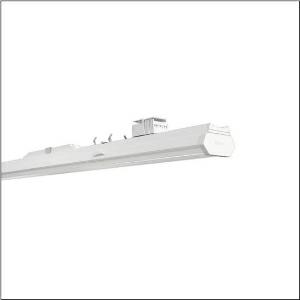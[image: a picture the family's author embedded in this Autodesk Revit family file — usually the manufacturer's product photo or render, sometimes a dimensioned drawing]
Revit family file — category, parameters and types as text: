
# Revit family: licross_21_protected_mo_52td1bdn4axg
name_source: partatom
category: Lighting Fixtures
units: mm (PartAtom-declared; Revit-internal decimal feet)

## family parameters
Cut with Voids When Loaded = No
Host = Face
Light Source = No
Part Type = Normal
Room Calculation Point = No
Round Connector Dimension = Use Diameter
Shared = No

## types (1)
- --- (1 x LED, 10050 lm, 62 W, 4000K)
    Apparent Load = 62 VA
    CIE Flux Codes = 54 82 95 97 100
    Color Rendering = 80
    Color Temperature = 4000K
    Default Elevation = 1800 mm
    Description = Licross 21 Protected MO, luminaire insert, of sheet steel, galvanised, coil coated, white, length: 1.500mm, width: 90mm, height: 103mm, LED rated luminous flux: 10.060lm, light colour: 840, SDCM (Standard Deviation of Colour Matching)MacAdam ≤ 3 SDCM (initial), control gear: DALI 2, with plug, 5-pole, with phase selection, mains connection: 220..240V, AC, 50/60Hz, rated input power: 62W, internal wiring halogen-free, primary optical cover: cover, of PMMA, light emission: direct distribution, primary light characteristic: symmetric, protection rating (complete): IP54, insulation class (complete): insulation class I (protective earthing), certification: CE, ENEC, VDE, UKCA, protection symbol: D if used in an environment with non-conductive dust loads with corresponding accessories, impact resistance: IK06, permissible ambient temperature for indoor applications: -25..+35°C, corresponds to IFS (International Featured Standards) requirements for safety and quality in the food industry, reducing of maximum allowable ambient temperature of 5°C with ceiling mounting, LABS conformity tested according to VDMA 24364:2018-05, The light source and the operating device comply with the requirements of the Ecodesign Regulation (EU) 2019/2020 and are replaceable in accordance with this regulation, packaging unit: 1 piece
    Height = 92 mm
    Lamp = 1 x LED
    Lamp Light Flux = 10050 lm
    Lamp Power = 62 W
    Lamp count = 1
    Length = 1500 mm
    Luminous efficacy = 162 lm/W
    Manufacturer = Siteco
    ModVariant = No
    Model = 52TD1BDN4AXG
    Mounting Place = Ceiling
    Mounting Type = Pendant
    Number of Poles = 1
    OnlyDefault = Yes
    Power Factor = 1
    Product Name = Licross 21 Protected MO
    Product group = luminaire insert | ceiling pendant
    ProductGroupID = 901
    Protection Class = Protection class I
    Protection Degree = IP 54
    RLX_Detail_Level = 1
    RLX_Emergency_Light_Flux = 0 lm
    RLX_Emergency_Type = 0
    RLX_Emergency_Type_DB = No
    RlxData = <blob elided: 24593 chars, md5=493fe9eb>
    Socket = socket
    Standby Power = 0 W
    System Light Flux = 10050 lm
    System Power = 62 W
    Type Comments = factory setting: luminous flux: 100 % | dim-lin: 254 | 418 mA
    Type Image = l_1256148.jpg
    URL = http://relux.com
    VarID = @adj_129221
    Voltage = 0 V
    Weight = 0.00 kg
    Width = 88 mm

## geometry (parser evidence)
native form markers: Blend x4, Sweep x11
no freeform markers — native parametric forms only
